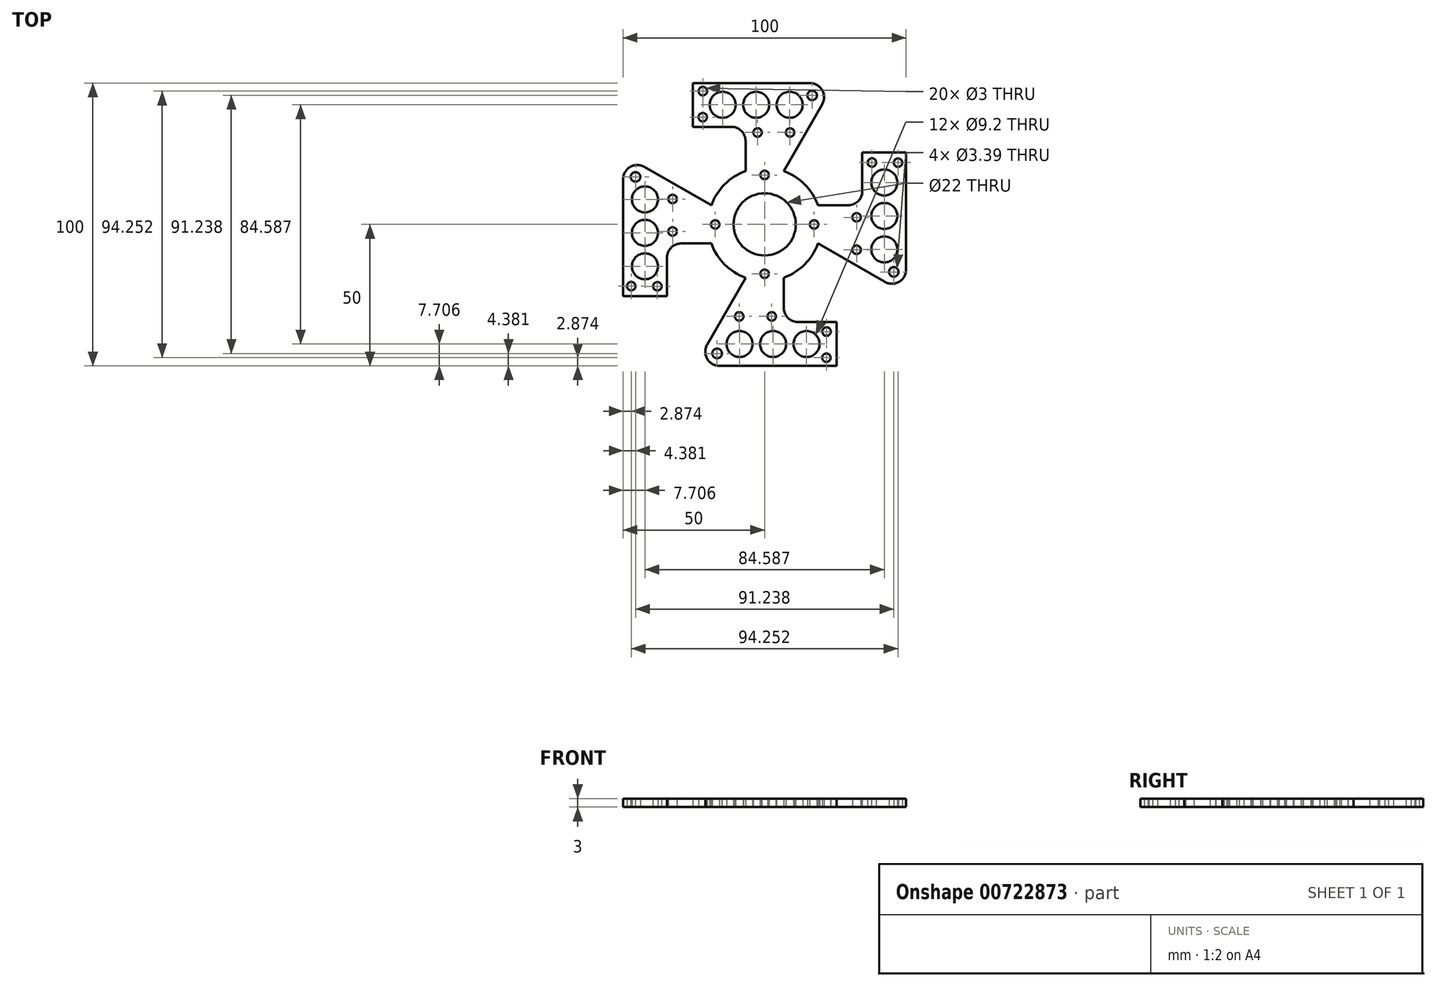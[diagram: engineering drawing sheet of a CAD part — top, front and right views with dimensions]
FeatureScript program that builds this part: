
annotation { "Feature Type Name" : "Feature", "Feature Type Description" : "" }
export const myFeature = defineFeature(function(context is Context, id is Id, definition is map)
    precondition{}
    {
        {
            var Q0;
            Q0=qCreatedBy(makeId("Top.planeOp"),FACE);
            var sketch = newSketch(context, id + "F0", { "sketchPlane" : qUnion([Q0])});
            skArc(sketch, "E0", {"start": v(7.78, 7.78) * mm, "mid": v(0, 11) * mm, "end": v(-7.78, 7.78) * mm});
            skArc(sketch, "E1", {"start": v(-6.75, 18.83) * mm, "mid": v(-10.7, 16.9) * mm, "end": v(-14.14, 14.14) * mm});
            skLineSegment(sketch, "E2", {"start": v(15.98, 50) * mm, "end": v(-25.39, 50) * mm});
            skLineSegment(sketch, "E3", {"start": v(-25.39, 50) * mm, "end": v(-25.39, 34.5) * mm});
            skLineSegment(sketch, "E4", {"start": v(-25.39, 34.5) * mm, "end": v(-11.75, 34.5) * mm});
            skPoint(sketch, "E5.orphan", {"position": v(3.2, 34.5) * mm});
            skLineSegment(sketch, "E6.trimOffspring", {"start": v(-6.75, 18.83) * mm, "end": v(-6.75, 29.5) * mm});
            skLineSegment(sketch, "E7.trimOffspring", {"start": v(6.75, 18.83) * mm, "end": v(20.32, 42.51) * mm});
            skPoint(sketch, "E8.end.orphan", {"position": v(-6.75, 0) * mm});
            skPoint(sketch, "E9.start.orphan", {"position": v(3.2, -2) * mm});
            skArc(sketch, "E10.trimOffspring", {"start": v(14.14, 14.14) * mm, "mid": v(10.7, 16.9) * mm, "end": v(6.75, 18.83) * mm});
            skLineSegment(sketch, "E11.1.0", {"start": v(-18.83, -6.75) * mm, "end": v(-29.5, -6.75) * mm});
            skLineSegment(sketch, "E11.1.1", {"start": v(-50, -25.39) * mm, "end": v(-34.5, -25.39) * mm});
            skArc(sketch, "E11.1.2", {"start": v(-14.14, 14.14) * mm, "mid": v(-16.9, 10.7) * mm, "end": v(-18.83, 6.75) * mm});
            skPoint(sketch, "E11.1.3", {"position": v(0, -6.75) * mm});
            skLineSegment(sketch, "E11.1.4", {"start": v(-50, 15.98) * mm, "end": v(-50, -25.39) * mm});
            skPoint(sketch, "E11.1.5", {"position": v(-34.5, 3.2) * mm});
            skPoint(sketch, "E11.1.6", {"position": v(2, 3.2) * mm});
            skArc(sketch, "E11.1.7", {"start": v(-18.83, -6.75) * mm, "mid": v(-16.9, -10.7) * mm, "end": v(-14.14, -14.14) * mm});
            skArc(sketch, "E11.1.8", {"start": v(-7.78, 7.78) * mm, "mid": v(-11, 0) * mm, "end": v(-7.78, -7.78) * mm});
            skLineSegment(sketch, "E11.1.9", {"start": v(-34.5, -25.39) * mm, "end": v(-34.5, -11.75) * mm});
            skLineSegment(sketch, "E11.1.10", {"start": v(-18.83, 6.75) * mm, "end": v(-42.51, 20.32) * mm});
            skLineSegment(sketch, "E11.2.0", {"start": v(6.75, -18.83) * mm, "end": v(6.75, -29.5) * mm});
            skLineSegment(sketch, "E11.2.1", {"start": v(25.39, -50) * mm, "end": v(25.39, -34.5) * mm});
            skArc(sketch, "E11.2.2", {"start": v(-14.14, -14.14) * mm, "mid": v(-10.7, -16.9) * mm, "end": v(-6.75, -18.83) * mm});
            skPoint(sketch, "E11.2.3", {"position": v(6.75, 0) * mm});
            skLineSegment(sketch, "E11.2.4", {"start": v(-15.98, -50) * mm, "end": v(25.39, -50) * mm});
            skPoint(sketch, "E11.2.5", {"position": v(-3.2, -34.5) * mm});
            skPoint(sketch, "E11.2.6", {"position": v(-3.2, 2) * mm});
            skArc(sketch, "E11.2.7", {"start": v(6.75, -18.83) * mm, "mid": v(10.7, -16.9) * mm, "end": v(14.14, -14.14) * mm});
            skArc(sketch, "E11.2.8", {"start": v(-7.78, -7.78) * mm, "mid": v(0, -11) * mm, "end": v(7.78, -7.78) * mm});
            skLineSegment(sketch, "E11.2.9", {"start": v(25.39, -34.5) * mm, "end": v(11.75, -34.5) * mm});
            skLineSegment(sketch, "E11.2.10", {"start": v(-6.75, -18.83) * mm, "end": v(-20.32, -42.51) * mm});
            skLineSegment(sketch, "E11.3.0", {"start": v(18.83, 6.75) * mm, "end": v(29.5, 6.75) * mm});
            skLineSegment(sketch, "E11.3.1", {"start": v(50, 25.39) * mm, "end": v(34.5, 25.39) * mm});
            skArc(sketch, "E11.3.2", {"start": v(14.14, -14.14) * mm, "mid": v(16.9, -10.7) * mm, "end": v(18.83, -6.75) * mm});
            skPoint(sketch, "E11.3.3", {"position": v(0, 6.75) * mm});
            skLineSegment(sketch, "E11.3.4", {"start": v(50, -15.98) * mm, "end": v(50, 25.39) * mm});
            skPoint(sketch, "E11.3.5", {"position": v(34.5, -3.2) * mm});
            skPoint(sketch, "E11.3.6", {"position": v(-2, -3.2) * mm});
            skArc(sketch, "E11.3.7", {"start": v(18.83, 6.75) * mm, "mid": v(16.9, 10.7) * mm, "end": v(14.14, 14.14) * mm});
            skArc(sketch, "E11.3.8", {"start": v(7.78, -7.78) * mm, "mid": v(11, 0) * mm, "end": v(7.78, 7.78) * mm});
            skLineSegment(sketch, "E11.3.9", {"start": v(34.5, 25.39) * mm, "end": v(34.5, 11.75) * mm});
            skLineSegment(sketch, "E11.3.10", {"start": v(18.83, -6.75) * mm, "end": v(42.51, -20.32) * mm});
            skPoint(sketch, "E12.visualSharp", {"position": v(-6.75, 34.5) * mm});
            skArc(sketch, "E12.filletArc", {"start": v(-6.75, 29.5) * mm, "mid": v(-8.21, 33.04) * mm, "end": v(-11.75, 34.5) * mm});
            skPoint(sketch, "E13.visualSharp", {"position": v(-34.5, -6.75) * mm});
            skArc(sketch, "E13.filletArc", {"start": v(-29.5, -6.75) * mm, "mid": v(-33.04, -8.21) * mm, "end": v(-34.5, -11.75) * mm});
            skPoint(sketch, "E14.visualSharp", {"position": v(6.75, -34.5) * mm});
            skArc(sketch, "E14.filletArc", {"start": v(6.75, -29.5) * mm, "mid": v(8.21, -33.04) * mm, "end": v(11.75, -34.5) * mm});
            skPoint(sketch, "E15.visualSharp", {"position": v(34.5, 6.75) * mm});
            skArc(sketch, "E15.filletArc", {"start": v(29.5, 6.75) * mm, "mid": v(33.04, 8.21) * mm, "end": v(34.5, 11.75) * mm});
            skPoint(sketch, "E16.visualSharp", {"position": v(-50, 24.61) * mm});
            skArc(sketch, "E16.filletArc", {"start": v(-42.51, 20.32) * mm, "mid": v(-47.5, 20.3) * mm, "end": v(-50, 15.98) * mm});
            skPoint(sketch, "E17.visualSharp", {"position": v(24.61, 50) * mm});
            skArc(sketch, "E17.filletArc", {"start": v(20.32, 42.51) * mm, "mid": v(20.3, 47.5) * mm, "end": v(15.98, 50) * mm});
            skPoint(sketch, "E18.visualSharp", {"position": v(-24.61, -50) * mm});
            skArc(sketch, "E18.filletArc", {"start": v(-20.32, -42.51) * mm, "mid": v(-20.3, -47.5) * mm, "end": v(-15.98, -50) * mm});
            skPoint(sketch, "E19.visualSharp", {"position": v(50, -24.61) * mm});
            skArc(sketch, "E19.filletArc", {"start": v(42.51, -20.32) * mm, "mid": v(47.5, -20.3) * mm, "end": v(50, -15.98) * mm});
            skSolve(sketch);
        }
        {
            var Q0;
            Q0 = qSketchRegion(id + "F0", true);
            extrude(context, id + "F1", {"entities" : qUnion([Q0]), "depth" : 3 * mm, "offsetDistance" : 25 * mm});
        }
        {
            var Q0;
            Q0=qCreatedBy(makeId("Top.planeOp"),FACE);
            var sketch = newSketch(context, id + "F2", { "sketchPlane" : qUnion([Q0])});
            skCircle(sketch, "E20", {"center": v(-14.82, 42.3) * mm, "radius": 4.6 * mm});
            skCircle(sketch, "E21", {"center": v(-2.98, 42.3) * mm, "radius": 4.6 * mm});
            skCircle(sketch, "E22", {"center": v(8.86, 42.3) * mm, "radius": 4.6 * mm});
            skCircle(sketch, "E23.1.0", {"center": v(-42.3, -2.98) * mm, "radius": 4.6 * mm});
            skCircle(sketch, "E23.1.1", {"center": v(-42.3, 8.86) * mm, "radius": 4.6 * mm});
            skCircle(sketch, "E23.1.2", {"center": v(-42.3, -14.82) * mm, "radius": 4.6 * mm});
            skCircle(sketch, "E23.2.0", {"center": v(2.98, -42.3) * mm, "radius": 4.6 * mm});
            skCircle(sketch, "E23.2.1", {"center": v(-8.86, -42.3) * mm, "radius": 4.6 * mm});
            skCircle(sketch, "E23.2.2", {"center": v(14.82, -42.3) * mm, "radius": 4.6 * mm});
            skCircle(sketch, "E23.3.0", {"center": v(42.3, 2.98) * mm, "radius": 4.6 * mm});
            skCircle(sketch, "E23.3.1", {"center": v(42.3, -8.86) * mm, "radius": 4.6 * mm});
            skCircle(sketch, "E23.3.2", {"center": v(42.3, 14.82) * mm, "radius": 4.6 * mm});
            skPoint(sketch, "E23.center", {"position": v(0, 0) * mm});
            skSolve(sketch);
        }
        {
            var Q0;
            Q0 = qSketchRegion(id + "F2", true);
            extrude(context, id + "F3", {"entities" : qUnion([Q0]), "operationType" : NewBodyOperationType.REMOVE, "depth" : 25 * mm, "offsetDistance" : 25 * mm});
        }
        {
            var Q0;
            Q0=qCreatedBy(makeId("Top.planeOp"),FACE);
            var sketch = newSketch(context, id + "F4", { "sketchPlane" : qUnion([Q0])});
            skCircle(sketch, "E24", {"center": v(16.8, 45.62) * mm, "radius": 1.7 * mm});
            skCircle(sketch, "E25", {"center": v(-21.83, 47.13) * mm, "radius": 1.5 * mm});
            skCircle(sketch, "E26", {"center": v(-21.88, 37.9) * mm, "radius": 1.5 * mm});
            skCircle(sketch, "E27", {"center": v(8.98, 32.5) * mm, "radius": 1.5 * mm});
            skCircle(sketch, "E28", {"center": v(0, 17.47) * mm, "radius": 1.5 * mm});
            skCircle(sketch, "E29", {"center": v(-2.5, 32.5) * mm, "radius": 1.5 * mm});
            skPoint(sketch, "E30.end.orphan", {"position": v(-13.99, 32.5) * mm});
            skPoint(sketch, "E31.1.0", {"position": v(-32.5, -13.99) * mm});
            skCircle(sketch, "E31.1.1", {"center": v(-32.5, -2.5) * mm, "radius": 1.5 * mm});
            skCircle(sketch, "E31.1.2", {"center": v(-37.9, -21.88) * mm, "radius": 1.5 * mm});
            skCircle(sketch, "E31.1.3", {"center": v(-45.62, 16.8) * mm, "radius": 1.7 * mm});
            skCircle(sketch, "E31.1.4", {"center": v(-32.5, 8.98) * mm, "radius": 1.5 * mm});
            skCircle(sketch, "E31.1.5", {"center": v(-47.13, -21.83) * mm, "radius": 1.5 * mm});
            skCircle(sketch, "E31.1.6", {"center": v(-17.47, 0) * mm, "radius": 1.5 * mm});
            skPoint(sketch, "E31.2.0", {"position": v(13.99, -32.5) * mm});
            skCircle(sketch, "E31.2.1", {"center": v(2.5, -32.5) * mm, "radius": 1.5 * mm});
            skCircle(sketch, "E31.2.2", {"center": v(21.88, -37.9) * mm, "radius": 1.5 * mm});
            skCircle(sketch, "E31.2.3", {"center": v(-16.8, -45.62) * mm, "radius": 1.7 * mm});
            skCircle(sketch, "E31.2.4", {"center": v(-8.98, -32.5) * mm, "radius": 1.5 * mm});
            skCircle(sketch, "E31.2.5", {"center": v(21.83, -47.13) * mm, "radius": 1.5 * mm});
            skCircle(sketch, "E31.2.6", {"center": v(0, -17.47) * mm, "radius": 1.5 * mm});
            skPoint(sketch, "E31.3.0", {"position": v(32.5, 13.99) * mm});
            skCircle(sketch, "E31.3.1", {"center": v(32.5, 2.5) * mm, "radius": 1.5 * mm});
            skCircle(sketch, "E31.3.2", {"center": v(37.9, 21.88) * mm, "radius": 1.5 * mm});
            skCircle(sketch, "E31.3.3", {"center": v(45.62, -16.8) * mm, "radius": 1.7 * mm});
            skCircle(sketch, "E31.3.4", {"center": v(32.5, -8.98) * mm, "radius": 1.5 * mm});
            skCircle(sketch, "E31.3.5", {"center": v(47.13, 21.83) * mm, "radius": 1.5 * mm});
            skCircle(sketch, "E31.3.6", {"center": v(17.47, 0) * mm, "radius": 1.5 * mm});
            skPoint(sketch, "E31.center", {"position": v(0, 0) * mm});
            skSolve(sketch);
        }
        {
            var Q0;
            Q0 = qSketchRegion(id + "F4", true);
            var Q1;
            Q1 = qConstructionFilter(qBodyType(qCreatedBy(id + "F4" ,EDGE), BodyType.WIRE), ConstructionObject.NO);
            extrude(context, id + "F5", {"entities" : qUnion([Q0]), "operationType" : NewBodyOperationType.REMOVE, "surfaceEntities" : qUnion([Q1]), "depth" : 30 * mm, "offsetDistance" : 25 * mm});
        }
    });
